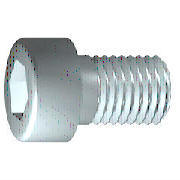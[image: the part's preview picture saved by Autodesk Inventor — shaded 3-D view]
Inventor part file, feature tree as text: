
AUTODESK INVENTOR PART (.ipt)
format: ipt  version: 2024.1 (Build 281209000, 209)  size: 194,048 bytes
history: native  units: mm (DEFAULTED — no unit token found)
features: extrude x1, plane x1, fillet x1
ambient origin geometry x7: Origin, YZ Plane, XY Plane, X Axis, Y Axis, Z Axis, Center Point
bodies: Solid1 (feature_tree), Body (feature_tree)
feature tree (3):
  extrude  "Slot"  Depth=6.75mm
  plane  "Work Plane1"
  fillet  "Fillet2"  Radius=0.306825mm
